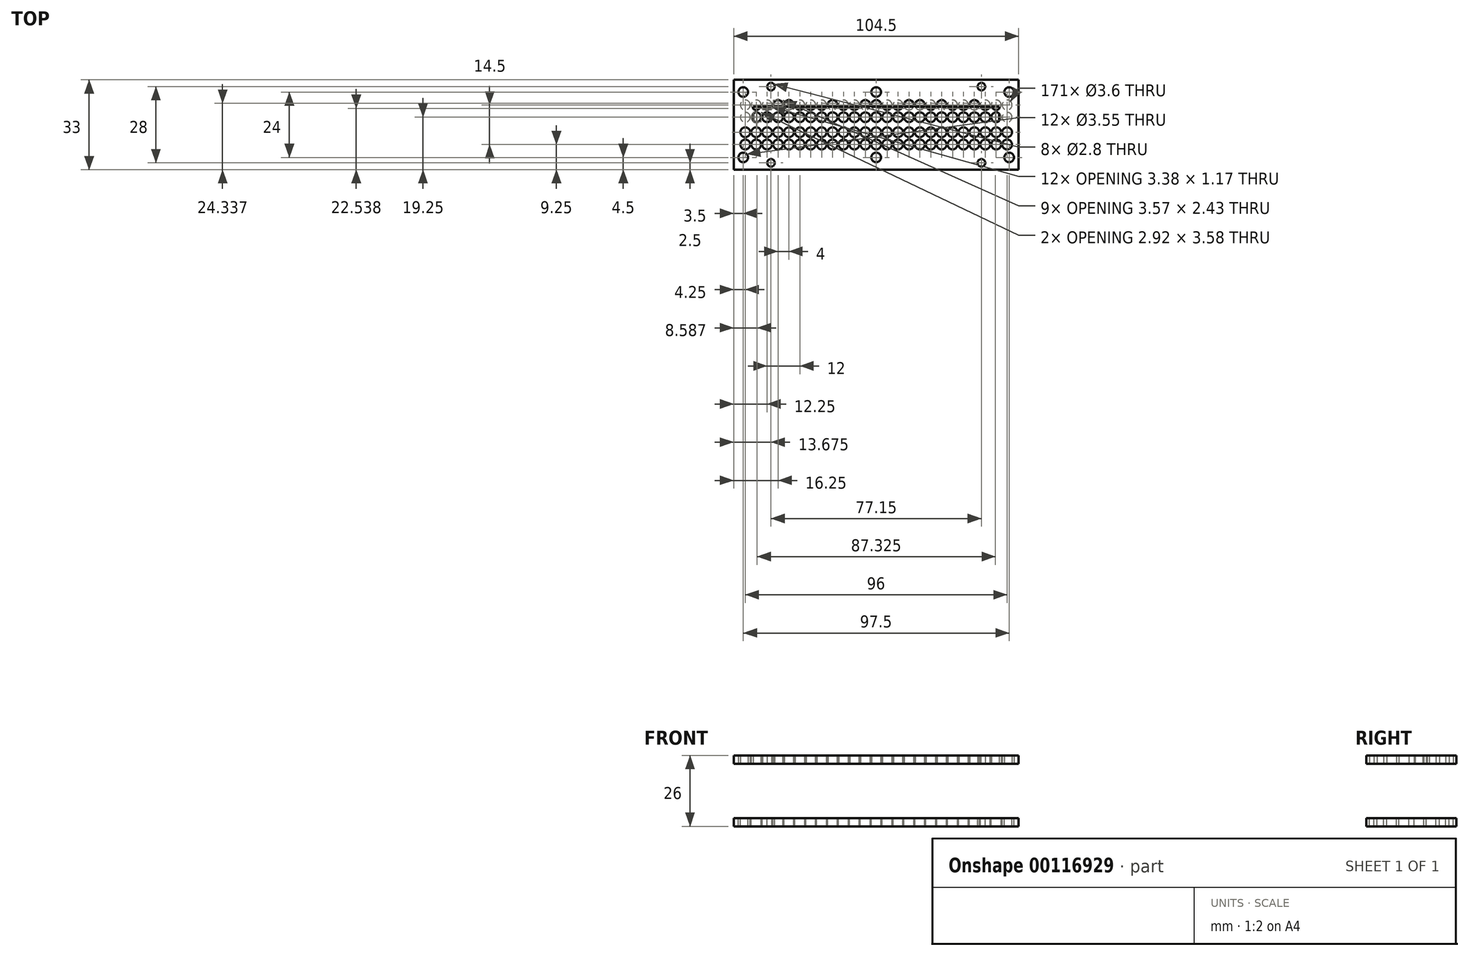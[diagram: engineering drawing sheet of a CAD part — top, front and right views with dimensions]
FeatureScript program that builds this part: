
annotation { "Feature Type Name" : "Feature", "Feature Type Description" : "" }
export const myFeature = defineFeature(function(context is Context, id is Id, definition is map)
    precondition{}
    {
        {
            var Q0;
            Q0=qCreatedBy(makeId("Top.planeOp"),FACE);
            cPlane(context, id + "F0", {"entities" : qUnion([Q0]), "cplaneType" : CPlaneType.OFFSET, "offset" : 25 * mm, "oppositeDirection" : true, "width" : 150 * mm, "height" : 150 * mm});
        }
        {
            var Q0;
            Q0=qCreatedBy(id+"F0.planeOp",FACE);
            var sketch = newSketch(context, id + "F1", { "sketchPlane" : qUnion([Q0])});
            skCircle(sketch, "E0", {"center": v(0, 12) * mm, "radius": 1.77 * mm});
            skCircle(sketch, "E1", {"center": v(-48.75, 12) * mm, "radius": 1.77 * mm});
            skCircle(sketch, "E2.MirrorC", {"center": v(48.75, 12) * mm, "radius": 1.77 * mm});
            skCircle(sketch, "E3.MirrorC", {"center": v(48.75, -12) * mm, "radius": 1.77 * mm});
            skCircle(sketch, "E4.MirrorC", {"center": v(0, -12) * mm, "radius": 1.77 * mm});
            skCircle(sketch, "E5.MirrorC", {"center": v(-48.75, -12) * mm, "radius": 1.77 * mm});
            skCircle(sketch, "E6", {"center": v(-48, 7.25) * mm, "radius": 1.8 * mm});
            skCircle(sketch, "E7.0.1.0", {"center": v(-48, 2.75) * mm, "radius": 1.8 * mm});
            skCircle(sketch, "E7.1.0.0", {"center": v(-44, 7.25) * mm, "radius": 1.8 * mm});
            skCircle(sketch, "E7.1.1.0", {"center": v(-44, 2.75) * mm, "radius": 1.8 * mm});
            skCircle(sketch, "E7.2.0.0", {"center": v(-40, 7.25) * mm, "radius": 1.8 * mm});
            skCircle(sketch, "E7.2.1.0", {"center": v(-40, 2.75) * mm, "radius": 1.8 * mm});
            skCircle(sketch, "E7.3.0.0", {"center": v(-36, 7.25) * mm, "radius": 1.8 * mm});
            skCircle(sketch, "E7.3.1.0", {"center": v(-36, 2.75) * mm, "radius": 1.8 * mm});
            skCircle(sketch, "E7.4.0.0", {"center": v(-32, 7.25) * mm, "radius": 1.8 * mm});
            skCircle(sketch, "E7.4.1.0", {"center": v(-32, 2.75) * mm, "radius": 1.8 * mm});
            skCircle(sketch, "E7.5.0.0", {"center": v(-28, 7.25) * mm, "radius": 1.8 * mm});
            skCircle(sketch, "E7.5.1.0", {"center": v(-28, 2.75) * mm, "radius": 1.8 * mm});
            skCircle(sketch, "E7.6.0.0", {"center": v(-24, 7.25) * mm, "radius": 1.8 * mm});
            skCircle(sketch, "E7.6.1.0", {"center": v(-24, 2.75) * mm, "radius": 1.8 * mm});
            skCircle(sketch, "E7.7.0.0", {"center": v(-20, 7.25) * mm, "radius": 1.8 * mm});
            skCircle(sketch, "E7.7.1.0", {"center": v(-20, 2.75) * mm, "radius": 1.8 * mm});
            skCircle(sketch, "E7.8.0.0", {"center": v(-16, 7.25) * mm, "radius": 1.8 * mm});
            skCircle(sketch, "E7.8.1.0", {"center": v(-16, 2.75) * mm, "radius": 1.8 * mm});
            skCircle(sketch, "E7.9.0.0", {"center": v(-12, 7.25) * mm, "radius": 1.8 * mm});
            skCircle(sketch, "E7.9.1.0", {"center": v(-12, 2.75) * mm, "radius": 1.8 * mm});
            skCircle(sketch, "E7.10.0.0", {"center": v(-8, 7.25) * mm, "radius": 1.8 * mm});
            skCircle(sketch, "E7.10.1.0", {"center": v(-8, 2.75) * mm, "radius": 1.8 * mm});
            skCircle(sketch, "E7.11.0.0", {"center": v(-4, 7.25) * mm, "radius": 1.8 * mm});
            skCircle(sketch, "E7.11.1.0", {"center": v(-4, 2.75) * mm, "radius": 1.8 * mm});
            skCircle(sketch, "E7.12.0.0", {"center": v(0, 7.25) * mm, "radius": 1.8 * mm});
            skCircle(sketch, "E7.12.1.0", {"center": v(0, 2.75) * mm, "radius": 1.8 * mm});
            skCircle(sketch, "E7.13.0.0", {"center": v(4, 7.25) * mm, "radius": 1.8 * mm});
            skCircle(sketch, "E7.13.1.0", {"center": v(4, 2.75) * mm, "radius": 1.8 * mm});
            skCircle(sketch, "E7.14.0.0", {"center": v(8, 7.25) * mm, "radius": 1.8 * mm});
            skCircle(sketch, "E7.14.1.0", {"center": v(8, 2.75) * mm, "radius": 1.8 * mm});
            skCircle(sketch, "E7.15.0.0", {"center": v(12, 7.25) * mm, "radius": 1.8 * mm});
            skCircle(sketch, "E7.15.1.0", {"center": v(12, 2.75) * mm, "radius": 1.8 * mm});
            skCircle(sketch, "E7.16.0.0", {"center": v(16, 7.25) * mm, "radius": 1.8 * mm});
            skCircle(sketch, "E7.16.1.0", {"center": v(16, 2.75) * mm, "radius": 1.8 * mm});
            skCircle(sketch, "E7.17.0.0", {"center": v(20, 7.25) * mm, "radius": 1.8 * mm});
            skCircle(sketch, "E7.17.1.0", {"center": v(20, 2.75) * mm, "radius": 1.8 * mm});
            skCircle(sketch, "E7.18.0.0", {"center": v(24, 7.25) * mm, "radius": 1.8 * mm});
            skCircle(sketch, "E7.18.1.0", {"center": v(24, 2.75) * mm, "radius": 1.8 * mm});
            skCircle(sketch, "E7.19.0.0", {"center": v(28, 7.25) * mm, "radius": 1.8 * mm});
            skCircle(sketch, "E7.19.1.0", {"center": v(28, 2.75) * mm, "radius": 1.8 * mm});
            skCircle(sketch, "E7.20.0.0", {"center": v(32, 7.25) * mm, "radius": 1.8 * mm});
            skCircle(sketch, "E7.20.1.0", {"center": v(32, 2.75) * mm, "radius": 1.8 * mm});
            skCircle(sketch, "E7.21.0.0", {"center": v(36, 7.25) * mm, "radius": 1.8 * mm});
            skCircle(sketch, "E7.21.1.0", {"center": v(36, 2.75) * mm, "radius": 1.8 * mm});
            skCircle(sketch, "E7.22.0.0", {"center": v(40, 7.25) * mm, "radius": 1.8 * mm});
            skCircle(sketch, "E7.22.1.0", {"center": v(40, 2.75) * mm, "radius": 1.8 * mm});
            skCircle(sketch, "E7.23.0.0", {"center": v(44, 7.25) * mm, "radius": 1.8 * mm});
            skCircle(sketch, "E7.23.1.0", {"center": v(44, 2.75) * mm, "radius": 1.8 * mm});
            skCircle(sketch, "E7.24.0.0", {"center": v(48, 7.25) * mm, "radius": 1.8 * mm});
            skCircle(sketch, "E7.24.1.0", {"center": v(48, 2.75) * mm, "radius": 1.8 * mm});
            skLineSegment(sketch, "E7.direction1", {"start": v(-48, 7.25) * mm, "end": v(-44, 7.25) * mm, "construction": true});
            skLineSegment(sketch, "E7.direction2", {"start": v(-48, 7.25) * mm, "end": v(-48, 2.75) * mm, "construction": true});
            skCircle(sketch, "E8.MirrorC", {"center": v(-24, -7.25) * mm, "radius": 1.8 * mm});
            skCircle(sketch, "E9.MirrorC", {"center": v(8, -7.25) * mm, "radius": 1.8 * mm});
            skCircle(sketch, "E10.MirrorC", {"center": v(40, -7.25) * mm, "radius": 1.8 * mm});
            skLineSegment(sketch, "E11.MirrorCS", {"start": v(-48, -7.25) * mm, "end": v(-44, -7.25) * mm, "construction": true});
            skLineSegment(sketch, "E12.MirrorCS", {"start": v(-48, -7.25) * mm, "end": v(-48, -2.75) * mm, "construction": true});
            skCircle(sketch, "E13.MirrorC", {"center": v(-12, -2.75) * mm, "radius": 1.8 * mm});
            skCircle(sketch, "E14.MirrorC", {"center": v(20, -2.75) * mm, "radius": 1.8 * mm});
            skCircle(sketch, "E15.MirrorC", {"center": v(-28, -2.75) * mm, "radius": 1.8 * mm});
            skCircle(sketch, "E16.MirrorC", {"center": v(4, -2.75) * mm, "radius": 1.8 * mm});
            skCircle(sketch, "E17.MirrorC", {"center": v(36, -2.75) * mm, "radius": 1.8 * mm});
            skCircle(sketch, "E18.MirrorC", {"center": v(-12, -7.25) * mm, "radius": 1.8 * mm});
            skCircle(sketch, "E19.MirrorC", {"center": v(20, -7.25) * mm, "radius": 1.8 * mm});
            skCircle(sketch, "E20.MirrorC", {"center": v(-36, -7.25) * mm, "radius": 1.8 * mm});
            skCircle(sketch, "E21.MirrorC", {"center": v(-40, -2.75) * mm, "radius": 1.8 * mm});
            skCircle(sketch, "E22.MirrorC", {"center": v(-40, -7.25) * mm, "radius": 1.8 * mm});
            skCircle(sketch, "E23.MirrorC", {"center": v(-44, -2.75) * mm, "radius": 1.8 * mm});
            skCircle(sketch, "E24.MirrorC", {"center": v(-44, -7.25) * mm, "radius": 1.8 * mm});
            skCircle(sketch, "E25.MirrorC", {"center": v(-48, -2.75) * mm, "radius": 1.8 * mm});
            skCircle(sketch, "E26.MirrorC", {"center": v(-28, -7.25) * mm, "radius": 1.8 * mm});
            skCircle(sketch, "E27.MirrorC", {"center": v(4, -7.25) * mm, "radius": 1.8 * mm});
            skCircle(sketch, "E28.MirrorC", {"center": v(36, -7.25) * mm, "radius": 1.8 * mm});
            skCircle(sketch, "E29.MirrorC", {"center": v(-48, -7.25) * mm, "radius": 1.8 * mm});
            skCircle(sketch, "E30.MirrorC", {"center": v(48, -2.75) * mm, "radius": 1.8 * mm});
            skCircle(sketch, "E31.MirrorC", {"center": v(-32, -2.75) * mm, "radius": 1.8 * mm});
            skCircle(sketch, "E32.MirrorC", {"center": v(-32, -7.25) * mm, "radius": 1.8 * mm});
            skCircle(sketch, "E33.MirrorC", {"center": v(-16, -2.75) * mm, "radius": 1.8 * mm});
            skCircle(sketch, "E34.MirrorC", {"center": v(16, -2.75) * mm, "radius": 1.8 * mm});
            skCircle(sketch, "E35.MirrorC", {"center": v(-36, -2.75) * mm, "radius": 1.8 * mm});
            skCircle(sketch, "E36.MirrorC", {"center": v(-16, -7.25) * mm, "radius": 1.8 * mm});
            skCircle(sketch, "E37.MirrorC", {"center": v(0, -2.75) * mm, "radius": 1.8 * mm});
            skCircle(sketch, "E38.MirrorC", {"center": v(16, -7.25) * mm, "radius": 1.8 * mm});
            skCircle(sketch, "E39.MirrorC", {"center": v(48, -7.25) * mm, "radius": 1.8 * mm});
            skCircle(sketch, "E40.MirrorC", {"center": v(32, -2.75) * mm, "radius": 1.8 * mm});
            skCircle(sketch, "E41.MirrorC", {"center": v(-20, -2.75) * mm, "radius": 1.8 * mm});
            skCircle(sketch, "E42.MirrorC", {"center": v(12, -2.75) * mm, "radius": 1.8 * mm});
            skCircle(sketch, "E43.MirrorC", {"center": v(0, -7.25) * mm, "radius": 1.8 * mm});
            skCircle(sketch, "E44.MirrorC", {"center": v(32, -7.25) * mm, "radius": 1.8 * mm});
            skCircle(sketch, "E45.MirrorC", {"center": v(44, -2.75) * mm, "radius": 1.8 * mm});
            skCircle(sketch, "E46.MirrorC", {"center": v(-4, -7.25) * mm, "radius": 1.8 * mm});
            skCircle(sketch, "E47.MirrorC", {"center": v(28, -7.25) * mm, "radius": 1.8 * mm});
            skCircle(sketch, "E48.MirrorC", {"center": v(-20, -7.25) * mm, "radius": 1.8 * mm});
            skCircle(sketch, "E49.MirrorC", {"center": v(-4, -2.75) * mm, "radius": 1.8 * mm});
            skCircle(sketch, "E50.MirrorC", {"center": v(12, -7.25) * mm, "radius": 1.8 * mm});
            skCircle(sketch, "E51.MirrorC", {"center": v(28, -2.75) * mm, "radius": 1.8 * mm});
            skCircle(sketch, "E52.MirrorC", {"center": v(44, -7.25) * mm, "radius": 1.8 * mm});
            skCircle(sketch, "E53.MirrorC", {"center": v(-8, -2.75) * mm, "radius": 1.8 * mm});
            skCircle(sketch, "E54.MirrorC", {"center": v(24, -2.75) * mm, "radius": 1.8 * mm});
            skCircle(sketch, "E55.MirrorC", {"center": v(24, -7.25) * mm, "radius": 1.8 * mm});
            skCircle(sketch, "E56.MirrorC", {"center": v(-8, -7.25) * mm, "radius": 1.8 * mm});
            skCircle(sketch, "E57.MirrorC", {"center": v(40, -2.75) * mm, "radius": 1.8 * mm});
            skCircle(sketch, "E58.MirrorC", {"center": v(8, -2.75) * mm, "radius": 1.8 * mm});
            skCircle(sketch, "E59.MirrorC", {"center": v(-24, -2.75) * mm, "radius": 1.8 * mm});
            skLineSegment(sketch, "E60.bottom", {"start": v(52.25, -16.5) * mm, "end": v(-52.25, -16.5) * mm});
            skLineSegment(sketch, "E60.top", {"start": v(52.25, 16.5) * mm, "end": v(-52.25, 16.5) * mm});
            skLineSegment(sketch, "E60.left", {"start": v(52.25, -16.5) * mm, "end": v(52.25, 16.5) * mm});
            skLineSegment(sketch, "E60.right", {"start": v(-52.25, -16.5) * mm, "end": v(-52.25, 16.5) * mm});
            skPoint(sketch, "E60.middle", {"position": v(0, 0) * mm});
            skLineSegment(sketch, "E61.bottom", {"start": v(45.12, -6.62) * mm, "end": v(-45.12, -6.63) * mm});
            skLineSegment(sketch, "E61.top", {"start": v(45.12, 6.63) * mm, "end": v(-45.12, 6.62) * mm});
            skLineSegment(sketch, "E61.left", {"start": v(45.12, -6.62) * mm, "end": v(45.12, 6.63) * mm});
            skLineSegment(sketch, "E61.right", {"start": v(-45.12, -6.63) * mm, "end": v(-45.12, 6.63) * mm});
            skCircle(sketch, "E62", {"center": v(-38.57, 14) * mm, "radius": 1.4 * mm});
            skCircle(sketch, "E63.MirrorC", {"center": v(38.57, 14) * mm, "radius": 1.4 * mm});
            skCircle(sketch, "E64.MirrorC", {"center": v(-38.57, -14) * mm, "radius": 1.4 * mm});
            skCircle(sketch, "E65.MirrorC", {"center": v(38.57, -14) * mm, "radius": 1.4 * mm});
            skSolve(sketch);
        }
        {
            var Q0;
            Q0=makeQuery(id+"F1.imprint","IMPRINT",FACE,{"disambiguationData":[TD([[makeQuery(id+"F1.imprint","IMPRINT",EDGE,{"derivedFrom":sQuery(id+"F1.wireOp",EDGE,"E6")}),-1.0]])]});
            var Q1;
            Q1=makeQuery(id+"F1.imprint","IMPRINT",FACE,{"disambiguationData":[TD([[makeQuery(id+"F1.imprint","IMPRINT",EDGE,{"derivedFrom":sQuery(id+"F1.wireOp",EDGE,"E0")}),-1.0]])]});
            var Q2;
            Q2=makeQuery(id+"F1.imprint","IMPRINT",FACE,{"disambiguationData":[TD([[makeQuery(id+"F1.imprint","IMPRINT",EDGE,{"derivedFrom":sQuery(id+"F1.wireOp",EDGE,"E7.2.1.0")}),-1.0]])]});
            extrude(context, id + "F2", {"entities" : qUnion([Q0, Q1, Q2]), "oppositeDirection" : true, "depth" : 3 * mm});
        }
        {
            var Q0;
            Q0=makeQuery(id+"F1.imprint","IMPRINT",FACE,{"disambiguationData":[TD([[makeQuery(id+"F1.imprint","IMPRINT",EDGE,{"derivedFrom":sQuery(id+"F1.wireOp",EDGE,"E0")}),-1.0]])]});
            var Q1;
            Q1=makeQuery(id+"F1.imprint","IMPRINT",FACE,{"disambiguationData":[TD([[makeQuery(id+"F1.imprint","IMPRINT",EDGE,{"derivedFrom":sQuery(id+"F1.wireOp",EDGE,"E6")}),1.0]])]});
            var Q2;
            {var subQ0=sQuery(id+"F1.wireOp",EDGE,"E61.top");var subQ1=sQuery(id+"F1.wireOp",EDGE,"E7.1.0.0");var subQ2=makeQuery(id+"F1.imprint","INTERSECT",VERTEX,{"derivedFrom":[subQ1,subQ0]});Q2=makeQuery(id+"F1.imprint","IMPRINT",FACE,{"disambiguationData":[TD([[makeQuery(id+"F1.imprint","IMPRINT",EDGE,{"disambiguationData":[TD([[subQ2,-1.0]])],"derivedFrom":subQ1}),1.0]])]});}
            var Q3;
            {var subQ0=sQuery(id+"F1.wireOp",EDGE,"E61.top");var subQ1=sQuery(id+"F1.wireOp",EDGE,"E7.2.0.0");var subQ2=makeQuery(id+"F1.imprint","INTERSECT",VERTEX,{"disambiguationData":[OD(0.0)],"derivedFrom":[subQ1,subQ0]});Q3=makeQuery(id+"F1.imprint","IMPRINT",FACE,{"disambiguationData":[TD([[makeQuery(id+"F1.imprint","IMPRINT",EDGE,{"disambiguationData":[TD([[subQ2,-1.0]])],"derivedFrom":subQ1}),1.0]])]});}
            var Q4;
            {var subQ0=sQuery(id+"F1.wireOp",EDGE,"E61.top");var subQ1=sQuery(id+"F1.wireOp",EDGE,"E7.3.0.0");var subQ2=makeQuery(id+"F1.imprint","INTERSECT",VERTEX,{"disambiguationData":[OD(0.0)],"derivedFrom":[subQ1,subQ0]});Q4=makeQuery(id+"F1.imprint","IMPRINT",FACE,{"disambiguationData":[TD([[makeQuery(id+"F1.imprint","IMPRINT",EDGE,{"disambiguationData":[TD([[subQ2,-1.0]])],"derivedFrom":subQ1}),1.0]])]});}
            var Q5;
            {var subQ0=sQuery(id+"F1.wireOp",EDGE,"E61.top");var subQ1=sQuery(id+"F1.wireOp",EDGE,"E7.4.0.0");var subQ2=makeQuery(id+"F1.imprint","INTERSECT",VERTEX,{"disambiguationData":[OD(0.0)],"derivedFrom":[subQ1,subQ0]});Q5=makeQuery(id+"F1.imprint","IMPRINT",FACE,{"disambiguationData":[TD([[makeQuery(id+"F1.imprint","IMPRINT",EDGE,{"disambiguationData":[TD([[subQ2,-1.0]])],"derivedFrom":subQ1}),1.0]])]});}
            var Q6;
            {var subQ0=sQuery(id+"F1.wireOp",EDGE,"E61.top");var subQ1=sQuery(id+"F1.wireOp",EDGE,"E7.5.0.0");var subQ2=makeQuery(id+"F1.imprint","INTERSECT",VERTEX,{"disambiguationData":[OD(0.0)],"derivedFrom":[subQ1,subQ0]});Q6=makeQuery(id+"F1.imprint","IMPRINT",FACE,{"disambiguationData":[TD([[makeQuery(id+"F1.imprint","IMPRINT",EDGE,{"disambiguationData":[TD([[subQ2,-1.0]])],"derivedFrom":subQ1}),1.0]])]});}
            var Q7;
            {var subQ0=sQuery(id+"F1.wireOp",EDGE,"E61.top");var subQ1=sQuery(id+"F1.wireOp",EDGE,"E7.6.0.0");var subQ2=makeQuery(id+"F1.imprint","INTERSECT",VERTEX,{"disambiguationData":[OD(0.0)],"derivedFrom":[subQ1,subQ0]});Q7=makeQuery(id+"F1.imprint","IMPRINT",FACE,{"disambiguationData":[TD([[makeQuery(id+"F1.imprint","IMPRINT",EDGE,{"disambiguationData":[TD([[subQ2,-1.0]])],"derivedFrom":subQ1}),1.0]])]});}
            var Q8;
            {var subQ0=sQuery(id+"F1.wireOp",EDGE,"E61.top");var subQ1=sQuery(id+"F1.wireOp",EDGE,"E7.7.0.0");var subQ2=makeQuery(id+"F1.imprint","INTERSECT",VERTEX,{"disambiguationData":[OD(0.0)],"derivedFrom":[subQ1,subQ0]});Q8=makeQuery(id+"F1.imprint","IMPRINT",FACE,{"disambiguationData":[TD([[makeQuery(id+"F1.imprint","IMPRINT",EDGE,{"disambiguationData":[TD([[subQ2,-1.0]])],"derivedFrom":subQ1}),1.0]])]});}
            var Q9;
            {var subQ0=sQuery(id+"F1.wireOp",EDGE,"E61.top");var subQ1=sQuery(id+"F1.wireOp",EDGE,"E7.8.0.0");var subQ2=makeQuery(id+"F1.imprint","INTERSECT",VERTEX,{"disambiguationData":[OD(0.0)],"derivedFrom":[subQ1,subQ0]});Q9=makeQuery(id+"F1.imprint","IMPRINT",FACE,{"disambiguationData":[TD([[makeQuery(id+"F1.imprint","IMPRINT",EDGE,{"disambiguationData":[TD([[subQ2,-1.0]])],"derivedFrom":subQ1}),1.0]])]});}
            var Q10;
            {var subQ0=sQuery(id+"F1.wireOp",EDGE,"E61.top");var subQ1=sQuery(id+"F1.wireOp",EDGE,"E7.9.0.0");var subQ2=makeQuery(id+"F1.imprint","INTERSECT",VERTEX,{"disambiguationData":[OD(0.0)],"derivedFrom":[subQ1,subQ0]});Q10=makeQuery(id+"F1.imprint","IMPRINT",FACE,{"disambiguationData":[TD([[makeQuery(id+"F1.imprint","IMPRINT",EDGE,{"disambiguationData":[TD([[subQ2,-1.0]])],"derivedFrom":subQ1}),1.0]])]});}
            var Q11;
            {var subQ0=sQuery(id+"F1.wireOp",EDGE,"E61.top");var subQ1=sQuery(id+"F1.wireOp",EDGE,"E7.10.0.0");var subQ2=makeQuery(id+"F1.imprint","INTERSECT",VERTEX,{"disambiguationData":[OD(0.0)],"derivedFrom":[subQ1,subQ0]});Q11=makeQuery(id+"F1.imprint","IMPRINT",FACE,{"disambiguationData":[TD([[makeQuery(id+"F1.imprint","IMPRINT",EDGE,{"disambiguationData":[TD([[subQ2,-1.0]])],"derivedFrom":subQ1}),1.0]])]});}
            var Q12;
            {var subQ0=sQuery(id+"F1.wireOp",EDGE,"E61.top");var subQ1=sQuery(id+"F1.wireOp",EDGE,"E7.11.0.0");var subQ2=makeQuery(id+"F1.imprint","INTERSECT",VERTEX,{"disambiguationData":[OD(0.0)],"derivedFrom":[subQ1,subQ0]});Q12=makeQuery(id+"F1.imprint","IMPRINT",FACE,{"disambiguationData":[TD([[makeQuery(id+"F1.imprint","IMPRINT",EDGE,{"disambiguationData":[TD([[subQ2,-1.0]])],"derivedFrom":subQ1}),1.0]])]});}
            var Q13;
            {var subQ0=sQuery(id+"F1.wireOp",EDGE,"E61.top");var subQ1=sQuery(id+"F1.wireOp",EDGE,"E7.12.0.0");var subQ2=makeQuery(id+"F1.imprint","INTERSECT",VERTEX,{"disambiguationData":[OD(0.0)],"derivedFrom":[subQ1,subQ0]});Q13=makeQuery(id+"F1.imprint","IMPRINT",FACE,{"disambiguationData":[TD([[makeQuery(id+"F1.imprint","IMPRINT",EDGE,{"disambiguationData":[TD([[subQ2,-1.0]])],"derivedFrom":subQ1}),1.0]])]});}
            var Q14;
            {var subQ0=sQuery(id+"F1.wireOp",EDGE,"E61.top");var subQ1=sQuery(id+"F1.wireOp",EDGE,"E7.13.0.0");var subQ2=makeQuery(id+"F1.imprint","INTERSECT",VERTEX,{"disambiguationData":[OD(0.0)],"derivedFrom":[subQ1,subQ0]});Q14=makeQuery(id+"F1.imprint","IMPRINT",FACE,{"disambiguationData":[TD([[makeQuery(id+"F1.imprint","IMPRINT",EDGE,{"disambiguationData":[TD([[subQ2,-1.0]])],"derivedFrom":subQ1}),1.0]])]});}
            var Q15;
            {var subQ0=sQuery(id+"F1.wireOp",EDGE,"E61.top");var subQ1=sQuery(id+"F1.wireOp",EDGE,"E7.14.0.0");var subQ2=makeQuery(id+"F1.imprint","INTERSECT",VERTEX,{"disambiguationData":[OD(0.0)],"derivedFrom":[subQ1,subQ0]});Q15=makeQuery(id+"F1.imprint","IMPRINT",FACE,{"disambiguationData":[TD([[makeQuery(id+"F1.imprint","IMPRINT",EDGE,{"disambiguationData":[TD([[subQ2,-1.0]])],"derivedFrom":subQ1}),1.0]])]});}
            var Q16;
            {var subQ0=sQuery(id+"F1.wireOp",EDGE,"E61.top");var subQ1=sQuery(id+"F1.wireOp",EDGE,"E7.15.0.0");var subQ2=makeQuery(id+"F1.imprint","INTERSECT",VERTEX,{"disambiguationData":[OD(0.0)],"derivedFrom":[subQ1,subQ0]});Q16=makeQuery(id+"F1.imprint","IMPRINT",FACE,{"disambiguationData":[TD([[makeQuery(id+"F1.imprint","IMPRINT",EDGE,{"disambiguationData":[TD([[subQ2,-1.0]])],"derivedFrom":subQ1}),1.0]])]});}
            var Q17;
            {var subQ0=sQuery(id+"F1.wireOp",EDGE,"E61.top");var subQ1=sQuery(id+"F1.wireOp",EDGE,"E7.16.0.0");var subQ2=makeQuery(id+"F1.imprint","INTERSECT",VERTEX,{"disambiguationData":[OD(0.0)],"derivedFrom":[subQ1,subQ0]});Q17=makeQuery(id+"F1.imprint","IMPRINT",FACE,{"disambiguationData":[TD([[makeQuery(id+"F1.imprint","IMPRINT",EDGE,{"disambiguationData":[TD([[subQ2,-1.0]])],"derivedFrom":subQ1}),1.0]])]});}
            var Q18;
            {var subQ0=sQuery(id+"F1.wireOp",EDGE,"E61.top");var subQ1=sQuery(id+"F1.wireOp",EDGE,"E7.17.0.0");var subQ2=makeQuery(id+"F1.imprint","INTERSECT",VERTEX,{"disambiguationData":[OD(0.0)],"derivedFrom":[subQ1,subQ0]});Q18=makeQuery(id+"F1.imprint","IMPRINT",FACE,{"disambiguationData":[TD([[makeQuery(id+"F1.imprint","IMPRINT",EDGE,{"disambiguationData":[TD([[subQ2,-1.0]])],"derivedFrom":subQ1}),1.0]])]});}
            var Q19;
            {var subQ0=sQuery(id+"F1.wireOp",EDGE,"E61.top");var subQ1=sQuery(id+"F1.wireOp",EDGE,"E7.18.0.0");var subQ2=makeQuery(id+"F1.imprint","INTERSECT",VERTEX,{"disambiguationData":[OD(0.0)],"derivedFrom":[subQ1,subQ0]});Q19=makeQuery(id+"F1.imprint","IMPRINT",FACE,{"disambiguationData":[TD([[makeQuery(id+"F1.imprint","IMPRINT",EDGE,{"disambiguationData":[TD([[subQ2,-1.0]])],"derivedFrom":subQ1}),1.0]])]});}
            var Q20;
            {var subQ0=sQuery(id+"F1.wireOp",EDGE,"E61.top");var subQ1=sQuery(id+"F1.wireOp",EDGE,"E7.19.0.0");var subQ2=makeQuery(id+"F1.imprint","INTERSECT",VERTEX,{"disambiguationData":[OD(0.0)],"derivedFrom":[subQ1,subQ0]});Q20=makeQuery(id+"F1.imprint","IMPRINT",FACE,{"disambiguationData":[TD([[makeQuery(id+"F1.imprint","IMPRINT",EDGE,{"disambiguationData":[TD([[subQ2,-1.0]])],"derivedFrom":subQ1}),1.0]])]});}
            var Q21;
            {var subQ0=sQuery(id+"F1.wireOp",EDGE,"E61.top");var subQ1=sQuery(id+"F1.wireOp",EDGE,"E7.20.0.0");var subQ2=makeQuery(id+"F1.imprint","INTERSECT",VERTEX,{"disambiguationData":[OD(0.0)],"derivedFrom":[subQ1,subQ0]});Q21=makeQuery(id+"F1.imprint","IMPRINT",FACE,{"disambiguationData":[TD([[makeQuery(id+"F1.imprint","IMPRINT",EDGE,{"disambiguationData":[TD([[subQ2,-1.0]])],"derivedFrom":subQ1}),1.0]])]});}
            var Q22;
            {var subQ0=sQuery(id+"F1.wireOp",EDGE,"E61.top");var subQ1=sQuery(id+"F1.wireOp",EDGE,"E7.21.0.0");var subQ2=makeQuery(id+"F1.imprint","INTERSECT",VERTEX,{"disambiguationData":[OD(0.0)],"derivedFrom":[subQ1,subQ0]});Q22=makeQuery(id+"F1.imprint","IMPRINT",FACE,{"disambiguationData":[TD([[makeQuery(id+"F1.imprint","IMPRINT",EDGE,{"disambiguationData":[TD([[subQ2,-1.0]])],"derivedFrom":subQ1}),1.0]])]});}
            var Q23;
            {var subQ0=sQuery(id+"F1.wireOp",EDGE,"E61.top");var subQ1=sQuery(id+"F1.wireOp",EDGE,"E7.22.0.0");var subQ2=makeQuery(id+"F1.imprint","INTERSECT",VERTEX,{"disambiguationData":[OD(0.0)],"derivedFrom":[subQ1,subQ0]});Q23=makeQuery(id+"F1.imprint","IMPRINT",FACE,{"disambiguationData":[TD([[makeQuery(id+"F1.imprint","IMPRINT",EDGE,{"disambiguationData":[TD([[subQ2,-1.0]])],"derivedFrom":subQ1}),1.0]])]});}
            var Q24;
            {var subQ0=sQuery(id+"F1.wireOp",EDGE,"E61.top");var subQ1=sQuery(id+"F1.wireOp",EDGE,"E7.23.0.0");var subQ2=makeQuery(id+"F1.imprint","INTERSECT",VERTEX,{"derivedFrom":[subQ1,subQ0]});Q24=makeQuery(id+"F1.imprint","IMPRINT",FACE,{"disambiguationData":[TD([[makeQuery(id+"F1.imprint","IMPRINT",EDGE,{"disambiguationData":[TD([[subQ2,1.0]])],"derivedFrom":subQ1}),1.0]])]});}
            var Q25;
            Q25=makeQuery(id+"F1.imprint","IMPRINT",FACE,{"disambiguationData":[TD([[makeQuery(id+"F1.imprint","IMPRINT",EDGE,{"derivedFrom":sQuery(id+"F1.wireOp",EDGE,"E7.24.0.0")}),1.0]])]});
            var Q26;
            Q26=makeQuery(id+"F1.imprint","IMPRINT",FACE,{"disambiguationData":[TD([[makeQuery(id+"F1.imprint","IMPRINT",EDGE,{"derivedFrom":sQuery(id+"F1.wireOp",EDGE,"E7.24.1.0")}),1.0]])]});
            var Q27;
            Q27=makeQuery(id+"F1.imprint","IMPRINT",FACE,{"disambiguationData":[TD([[makeQuery(id+"F1.imprint","IMPRINT",EDGE,{"derivedFrom":sQuery(id+"F1.wireOp",EDGE,"E30.MirrorC")}),-1.0]])]});
            var Q28;
            Q28=makeQuery(id+"F1.imprint","IMPRINT",FACE,{"disambiguationData":[TD([[makeQuery(id+"F1.imprint","IMPRINT",EDGE,{"derivedFrom":sQuery(id+"F1.wireOp",EDGE,"E39.MirrorC")}),-1.0]])]});
            var Q29;
            {var subQ0=sQuery(id+"F1.wireOp",EDGE,"E61.bottom");var subQ1=sQuery(id+"F1.wireOp",EDGE,"E52.MirrorC");var subQ2=makeQuery(id+"F1.imprint","INTERSECT",VERTEX,{"derivedFrom":[subQ1,subQ0]});Q29=makeQuery(id+"F1.imprint","IMPRINT",FACE,{"disambiguationData":[TD([[makeQuery(id+"F1.imprint","IMPRINT",EDGE,{"disambiguationData":[TD([[subQ2,1.0]])],"derivedFrom":subQ1}),-1.0]])]});}
            var Q30;
            {var subQ0=sQuery(id+"F1.wireOp",EDGE,"E61.left");var subQ1=sQuery(id+"F1.wireOp",EDGE,"E45.MirrorC");var subQ2=makeQuery(id+"F1.imprint","INTERSECT",VERTEX,{"disambiguationData":[OD(0.0)],"derivedFrom":[subQ1,subQ0]});Q30=makeQuery(id+"F1.imprint","IMPRINT",FACE,{"disambiguationData":[TD([[makeQuery(id+"F1.imprint","IMPRINT",EDGE,{"disambiguationData":[TD([[subQ2,1.0]])],"derivedFrom":subQ1}),-1.0]])]});}
            var Q31;
            {var subQ0=sQuery(id+"F1.wireOp",EDGE,"E61.left");var subQ1=sQuery(id+"F1.wireOp",EDGE,"E7.23.1.0");var subQ2=makeQuery(id+"F1.imprint","INTERSECT",VERTEX,{"disambiguationData":[OD(0.0)],"derivedFrom":[subQ1,subQ0]});Q31=makeQuery(id+"F1.imprint","IMPRINT",FACE,{"disambiguationData":[TD([[makeQuery(id+"F1.imprint","IMPRINT",EDGE,{"disambiguationData":[TD([[subQ2,-1.0]])],"derivedFrom":subQ1}),1.0]])]});}
            var Q32;
            {var subQ0=sQuery(id+"F1.wireOp",EDGE,"E61.bottom");var subQ1=sQuery(id+"F1.wireOp",EDGE,"E10.MirrorC");var subQ2=makeQuery(id+"F1.imprint","INTERSECT",VERTEX,{"disambiguationData":[OD(0.0)],"derivedFrom":[subQ1,subQ0]});Q32=makeQuery(id+"F1.imprint","IMPRINT",FACE,{"disambiguationData":[TD([[makeQuery(id+"F1.imprint","IMPRINT",EDGE,{"disambiguationData":[TD([[subQ2,-1.0]])],"derivedFrom":subQ1}),-1.0]])]});}
            var Q33;
            {var subQ0=sQuery(id+"F1.wireOp",EDGE,"E61.bottom");var subQ1=sQuery(id+"F1.wireOp",EDGE,"E28.MirrorC");var subQ2=makeQuery(id+"F1.imprint","INTERSECT",VERTEX,{"disambiguationData":[OD(0.0)],"derivedFrom":[subQ1,subQ0]});Q33=makeQuery(id+"F1.imprint","IMPRINT",FACE,{"disambiguationData":[TD([[makeQuery(id+"F1.imprint","IMPRINT",EDGE,{"disambiguationData":[TD([[subQ2,-1.0]])],"derivedFrom":subQ1}),-1.0]])]});}
            var Q34;
            {var subQ0=sQuery(id+"F1.wireOp",EDGE,"E61.bottom");var subQ1=sQuery(id+"F1.wireOp",EDGE,"E44.MirrorC");var subQ2=makeQuery(id+"F1.imprint","INTERSECT",VERTEX,{"disambiguationData":[OD(0.0)],"derivedFrom":[subQ1,subQ0]});Q34=makeQuery(id+"F1.imprint","IMPRINT",FACE,{"disambiguationData":[TD([[makeQuery(id+"F1.imprint","IMPRINT",EDGE,{"disambiguationData":[TD([[subQ2,-1.0]])],"derivedFrom":subQ1}),-1.0]])]});}
            var Q35;
            {var subQ0=sQuery(id+"F1.wireOp",EDGE,"E61.bottom");var subQ1=sQuery(id+"F1.wireOp",EDGE,"E47.MirrorC");var subQ2=makeQuery(id+"F1.imprint","INTERSECT",VERTEX,{"disambiguationData":[OD(0.0)],"derivedFrom":[subQ1,subQ0]});Q35=makeQuery(id+"F1.imprint","IMPRINT",FACE,{"disambiguationData":[TD([[makeQuery(id+"F1.imprint","IMPRINT",EDGE,{"disambiguationData":[TD([[subQ2,-1.0]])],"derivedFrom":subQ1}),-1.0]])]});}
            var Q36;
            {var subQ0=sQuery(id+"F1.wireOp",EDGE,"E61.bottom");var subQ1=sQuery(id+"F1.wireOp",EDGE,"E55.MirrorC");var subQ2=makeQuery(id+"F1.imprint","INTERSECT",VERTEX,{"disambiguationData":[OD(0.0)],"derivedFrom":[subQ1,subQ0]});Q36=makeQuery(id+"F1.imprint","IMPRINT",FACE,{"disambiguationData":[TD([[makeQuery(id+"F1.imprint","IMPRINT",EDGE,{"disambiguationData":[TD([[subQ2,-1.0]])],"derivedFrom":subQ1}),-1.0]])]});}
            var Q37;
            {var subQ0=sQuery(id+"F1.wireOp",EDGE,"E61.bottom");var subQ1=sQuery(id+"F1.wireOp",EDGE,"E19.MirrorC");var subQ2=makeQuery(id+"F1.imprint","INTERSECT",VERTEX,{"disambiguationData":[OD(0.0)],"derivedFrom":[subQ1,subQ0]});Q37=makeQuery(id+"F1.imprint","IMPRINT",FACE,{"disambiguationData":[TD([[makeQuery(id+"F1.imprint","IMPRINT",EDGE,{"disambiguationData":[TD([[subQ2,-1.0]])],"derivedFrom":subQ1}),-1.0]])]});}
            var Q38;
            {var subQ0=sQuery(id+"F1.wireOp",EDGE,"E61.bottom");var subQ1=sQuery(id+"F1.wireOp",EDGE,"E38.MirrorC");var subQ2=makeQuery(id+"F1.imprint","INTERSECT",VERTEX,{"disambiguationData":[OD(0.0)],"derivedFrom":[subQ1,subQ0]});Q38=makeQuery(id+"F1.imprint","IMPRINT",FACE,{"disambiguationData":[TD([[makeQuery(id+"F1.imprint","IMPRINT",EDGE,{"disambiguationData":[TD([[subQ2,-1.0]])],"derivedFrom":subQ1}),-1.0]])]});}
            var Q39;
            {var subQ0=sQuery(id+"F1.wireOp",EDGE,"E61.bottom");var subQ1=sQuery(id+"F1.wireOp",EDGE,"E50.MirrorC");var subQ2=makeQuery(id+"F1.imprint","INTERSECT",VERTEX,{"disambiguationData":[OD(0.0)],"derivedFrom":[subQ1,subQ0]});Q39=makeQuery(id+"F1.imprint","IMPRINT",FACE,{"disambiguationData":[TD([[makeQuery(id+"F1.imprint","IMPRINT",EDGE,{"disambiguationData":[TD([[subQ2,-1.0]])],"derivedFrom":subQ1}),-1.0]])]});}
            var Q40;
            {var subQ0=sQuery(id+"F1.wireOp",EDGE,"E61.bottom");var subQ1=sQuery(id+"F1.wireOp",EDGE,"E9.MirrorC");var subQ2=makeQuery(id+"F1.imprint","INTERSECT",VERTEX,{"disambiguationData":[OD(0.0)],"derivedFrom":[subQ1,subQ0]});Q40=makeQuery(id+"F1.imprint","IMPRINT",FACE,{"disambiguationData":[TD([[makeQuery(id+"F1.imprint","IMPRINT",EDGE,{"disambiguationData":[TD([[subQ2,-1.0]])],"derivedFrom":subQ1}),-1.0]])]});}
            var Q41;
            {var subQ0=sQuery(id+"F1.wireOp",EDGE,"E61.bottom");var subQ1=sQuery(id+"F1.wireOp",EDGE,"E27.MirrorC");var subQ2=makeQuery(id+"F1.imprint","INTERSECT",VERTEX,{"disambiguationData":[OD(0.0)],"derivedFrom":[subQ1,subQ0]});Q41=makeQuery(id+"F1.imprint","IMPRINT",FACE,{"disambiguationData":[TD([[makeQuery(id+"F1.imprint","IMPRINT",EDGE,{"disambiguationData":[TD([[subQ2,-1.0]])],"derivedFrom":subQ1}),-1.0]])]});}
            var Q42;
            {var subQ0=sQuery(id+"F1.wireOp",EDGE,"E61.bottom");var subQ1=sQuery(id+"F1.wireOp",EDGE,"E43.MirrorC");var subQ2=makeQuery(id+"F1.imprint","INTERSECT",VERTEX,{"disambiguationData":[OD(0.0)],"derivedFrom":[subQ1,subQ0]});Q42=makeQuery(id+"F1.imprint","IMPRINT",FACE,{"disambiguationData":[TD([[makeQuery(id+"F1.imprint","IMPRINT",EDGE,{"disambiguationData":[TD([[subQ2,-1.0]])],"derivedFrom":subQ1}),-1.0]])]});}
            var Q43;
            {var subQ0=sQuery(id+"F1.wireOp",EDGE,"E61.bottom");var subQ1=sQuery(id+"F1.wireOp",EDGE,"E46.MirrorC");var subQ2=makeQuery(id+"F1.imprint","INTERSECT",VERTEX,{"disambiguationData":[OD(0.0)],"derivedFrom":[subQ1,subQ0]});Q43=makeQuery(id+"F1.imprint","IMPRINT",FACE,{"disambiguationData":[TD([[makeQuery(id+"F1.imprint","IMPRINT",EDGE,{"disambiguationData":[TD([[subQ2,-1.0]])],"derivedFrom":subQ1}),-1.0]])]});}
            var Q44;
            {var subQ0=sQuery(id+"F1.wireOp",EDGE,"E61.bottom");var subQ1=sQuery(id+"F1.wireOp",EDGE,"E56.MirrorC");var subQ2=makeQuery(id+"F1.imprint","INTERSECT",VERTEX,{"disambiguationData":[OD(0.0)],"derivedFrom":[subQ1,subQ0]});Q44=makeQuery(id+"F1.imprint","IMPRINT",FACE,{"disambiguationData":[TD([[makeQuery(id+"F1.imprint","IMPRINT",EDGE,{"disambiguationData":[TD([[subQ2,-1.0]])],"derivedFrom":subQ1}),-1.0]])]});}
            var Q45;
            {var subQ0=sQuery(id+"F1.wireOp",EDGE,"E61.bottom");var subQ1=sQuery(id+"F1.wireOp",EDGE,"E18.MirrorC");var subQ2=makeQuery(id+"F1.imprint","INTERSECT",VERTEX,{"disambiguationData":[OD(0.0)],"derivedFrom":[subQ1,subQ0]});Q45=makeQuery(id+"F1.imprint","IMPRINT",FACE,{"disambiguationData":[TD([[makeQuery(id+"F1.imprint","IMPRINT",EDGE,{"disambiguationData":[TD([[subQ2,-1.0]])],"derivedFrom":subQ1}),-1.0]])]});}
            var Q46;
            {var subQ0=sQuery(id+"F1.wireOp",EDGE,"E61.bottom");var subQ1=sQuery(id+"F1.wireOp",EDGE,"E36.MirrorC");var subQ2=makeQuery(id+"F1.imprint","INTERSECT",VERTEX,{"disambiguationData":[OD(0.0)],"derivedFrom":[subQ1,subQ0]});Q46=makeQuery(id+"F1.imprint","IMPRINT",FACE,{"disambiguationData":[TD([[makeQuery(id+"F1.imprint","IMPRINT",EDGE,{"disambiguationData":[TD([[subQ2,-1.0]])],"derivedFrom":subQ1}),-1.0]])]});}
            var Q47;
            {var subQ0=sQuery(id+"F1.wireOp",EDGE,"E61.bottom");var subQ1=sQuery(id+"F1.wireOp",EDGE,"E48.MirrorC");var subQ2=makeQuery(id+"F1.imprint","INTERSECT",VERTEX,{"disambiguationData":[OD(0.0)],"derivedFrom":[subQ1,subQ0]});Q47=makeQuery(id+"F1.imprint","IMPRINT",FACE,{"disambiguationData":[TD([[makeQuery(id+"F1.imprint","IMPRINT",EDGE,{"disambiguationData":[TD([[subQ2,-1.0]])],"derivedFrom":subQ1}),-1.0]])]});}
            var Q48;
            {var subQ0=sQuery(id+"F1.wireOp",EDGE,"E61.bottom");var subQ1=sQuery(id+"F1.wireOp",EDGE,"E8.MirrorC");var subQ2=makeQuery(id+"F1.imprint","INTERSECT",VERTEX,{"disambiguationData":[OD(0.0)],"derivedFrom":[subQ1,subQ0]});Q48=makeQuery(id+"F1.imprint","IMPRINT",FACE,{"disambiguationData":[TD([[makeQuery(id+"F1.imprint","IMPRINT",EDGE,{"disambiguationData":[TD([[subQ2,-1.0]])],"derivedFrom":subQ1}),-1.0]])]});}
            var Q49;
            {var subQ0=sQuery(id+"F1.wireOp",EDGE,"E61.bottom");var subQ1=sQuery(id+"F1.wireOp",EDGE,"E26.MirrorC");var subQ2=makeQuery(id+"F1.imprint","INTERSECT",VERTEX,{"disambiguationData":[OD(0.0)],"derivedFrom":[subQ1,subQ0]});Q49=makeQuery(id+"F1.imprint","IMPRINT",FACE,{"disambiguationData":[TD([[makeQuery(id+"F1.imprint","IMPRINT",EDGE,{"disambiguationData":[TD([[subQ2,-1.0]])],"derivedFrom":subQ1}),-1.0]])]});}
            var Q50;
            {var subQ0=sQuery(id+"F1.wireOp",EDGE,"E61.bottom");var subQ1=sQuery(id+"F1.wireOp",EDGE,"E32.MirrorC");var subQ2=makeQuery(id+"F1.imprint","INTERSECT",VERTEX,{"disambiguationData":[OD(0.0)],"derivedFrom":[subQ1,subQ0]});Q50=makeQuery(id+"F1.imprint","IMPRINT",FACE,{"disambiguationData":[TD([[makeQuery(id+"F1.imprint","IMPRINT",EDGE,{"disambiguationData":[TD([[subQ2,-1.0]])],"derivedFrom":subQ1}),-1.0]])]});}
            var Q51;
            {var subQ0=sQuery(id+"F1.wireOp",EDGE,"E61.bottom");var subQ1=sQuery(id+"F1.wireOp",EDGE,"E20.MirrorC");var subQ2=makeQuery(id+"F1.imprint","INTERSECT",VERTEX,{"disambiguationData":[OD(0.0)],"derivedFrom":[subQ1,subQ0]});Q51=makeQuery(id+"F1.imprint","IMPRINT",FACE,{"disambiguationData":[TD([[makeQuery(id+"F1.imprint","IMPRINT",EDGE,{"disambiguationData":[TD([[subQ2,-1.0]])],"derivedFrom":subQ1}),-1.0]])]});}
            var Q52;
            {var subQ0=sQuery(id+"F1.wireOp",EDGE,"E61.bottom");var subQ1=sQuery(id+"F1.wireOp",EDGE,"E22.MirrorC");var subQ2=makeQuery(id+"F1.imprint","INTERSECT",VERTEX,{"disambiguationData":[OD(0.0)],"derivedFrom":[subQ1,subQ0]});Q52=makeQuery(id+"F1.imprint","IMPRINT",FACE,{"disambiguationData":[TD([[makeQuery(id+"F1.imprint","IMPRINT",EDGE,{"disambiguationData":[TD([[subQ2,-1.0]])],"derivedFrom":subQ1}),-1.0]])]});}
            var Q53;
            {var subQ0=sQuery(id+"F1.wireOp",EDGE,"E61.bottom");var subQ1=sQuery(id+"F1.wireOp",EDGE,"E24.MirrorC");var subQ2=makeQuery(id+"F1.imprint","INTERSECT",VERTEX,{"derivedFrom":[subQ1,subQ0]});Q53=makeQuery(id+"F1.imprint","IMPRINT",FACE,{"disambiguationData":[TD([[makeQuery(id+"F1.imprint","IMPRINT",EDGE,{"disambiguationData":[TD([[subQ2,-1.0]])],"derivedFrom":subQ1}),-1.0]])]});}
            var Q54;
            {var subQ0=sQuery(id+"F1.wireOp",EDGE,"E61.right");var subQ1=sQuery(id+"F1.wireOp",EDGE,"E23.MirrorC");var subQ2=makeQuery(id+"F1.imprint","INTERSECT",VERTEX,{"disambiguationData":[OD(0.0)],"derivedFrom":[subQ1,subQ0]});Q54=makeQuery(id+"F1.imprint","IMPRINT",FACE,{"disambiguationData":[TD([[makeQuery(id+"F1.imprint","IMPRINT",EDGE,{"disambiguationData":[TD([[subQ2,-1.0]])],"derivedFrom":subQ1}),-1.0]])]});}
            var Q55;
            {var subQ0=sQuery(id+"F1.wireOp",EDGE,"E61.right");var subQ1=sQuery(id+"F1.wireOp",EDGE,"E7.1.1.0");var subQ2=makeQuery(id+"F1.imprint","INTERSECT",VERTEX,{"disambiguationData":[OD(0.0)],"derivedFrom":[subQ1,subQ0]});Q55=makeQuery(id+"F1.imprint","IMPRINT",FACE,{"disambiguationData":[TD([[makeQuery(id+"F1.imprint","IMPRINT",EDGE,{"disambiguationData":[TD([[subQ2,1.0]])],"derivedFrom":subQ1}),1.0]])]});}
            var Q56;
            Q56=makeQuery(id+"F1.imprint","IMPRINT",FACE,{"disambiguationData":[TD([[makeQuery(id+"F1.imprint","IMPRINT",EDGE,{"derivedFrom":sQuery(id+"F1.wireOp",EDGE,"E7.0.1.0")}),1.0]])]});
            var Q57;
            Q57=makeQuery(id+"F1.imprint","IMPRINT",FACE,{"disambiguationData":[TD([[makeQuery(id+"F1.imprint","IMPRINT",EDGE,{"derivedFrom":sQuery(id+"F1.wireOp",EDGE,"E25.MirrorC")}),-1.0]])]});
            var Q58;
            Q58=makeQuery(id+"F1.imprint","IMPRINT",FACE,{"disambiguationData":[TD([[makeQuery(id+"F1.imprint","IMPRINT",EDGE,{"derivedFrom":sQuery(id+"F1.wireOp",EDGE,"E29.MirrorC")}),-1.0]])]});
            extrude(context, id + "F3", {"entities" : qUnion([Q0, Q1, Q2, Q3, Q4, Q5, Q6, Q7, Q8, Q9, Q10, Q11, Q12, Q13, Q14, Q15, Q16, Q17, Q18, Q19, Q20, Q21, Q22, Q23, Q24, Q25, Q26, Q27, Q28, Q29, Q30, Q31, Q32, Q33, Q34, Q35, Q36, Q37, Q38, Q39, Q40, Q41, Q42, Q43, Q44, Q45, Q46, Q47, Q48, Q49, Q50, Q51, Q52, Q53, Q54, Q55, Q56, Q57, Q58]), "depth" : 23 * mm, "hasSecondDirection" : true, "secondDirectionOppositeDirection" : false, "secondDirectionDepth" : 20 * mm});
        }
    });
